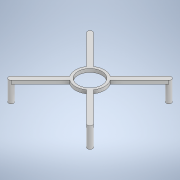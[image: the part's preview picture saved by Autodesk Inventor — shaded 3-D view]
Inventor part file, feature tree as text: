
AUTODESK INVENTOR PART (.ipt)
format: ipt  version: 2020 (Build 240168000, 168)  size: 166,400 bytes
history: native  units: mm
features: extrude x8, sketch x8
ambient origin geometry x8: Origin, YZ Plane, XZ Plane, XY Plane, X Axis, Y Axis, Z Axis, Center Point
bodies: Solid1 (feature_tree)
feature tree (16):
  extrude  "Extrusion1"  TaperAngle=45.0deg  [1 undecoded]
  extrude  "Extrusion2"  Depth=10.0mm TaperAngle=0.0deg
  extrude  "Extrusion3"  TaperAngle=45.0deg  [1 undecoded]
  extrude  "Extrusion4"  Depth=10.0mm TaperAngle=0.0deg
  extrude  "Extrusion5"  TaperAngle=135.0deg  [1 undecoded]
  extrude  "Extrusion6"  Depth=10.0mm TaperAngle=0.0deg
  extrude  "Extrusion7"  TaperAngle=45.0deg  [1 undecoded]
  extrude  "Extrusion8"  Depth=10.0mm TaperAngle=0.0deg
  sketch  "Sketch1"  dims[d0=32.75mm d1=45.0deg]
  sketch  "Sketch2"  dims[d2=3.0mm d3=10.0mm d4=0.0mm]
  sketch  "Sketch3"  dims[d5=32.75mm d6=45.0deg]
  sketch  "Sketch4"  dims[d7=3.0mm d8=10.0mm d9=0.0mm]
  sketch  "Sketch5"  dims[d10=32.75mm d11=135.0deg]
  sketch  "Sketch6"  dims[d12=3.0mm d13=10.0mm d14=0.0mm]
  sketch  "Sketch7"  dims[d15=32.75mm d16=45.0deg]
  sketch  "Sketch8"  dims[d17=3.0mm d18=10.0mm d19=0.0mm d20=3.0mm d21=2.0mm d22=0.0mm d23=3.0mm d24=2.0mm d25=0.0mm d26=17.0mm d27=2.0mm d28=0.0mm d29=14.0mm d30=2.0mm d31=0.0mm]
note: 4 required parameter values undecoded (feature->parameter linkage not recoverable at this tier; creation-order binding heuristic only, values carry confidence <= 0.55)
